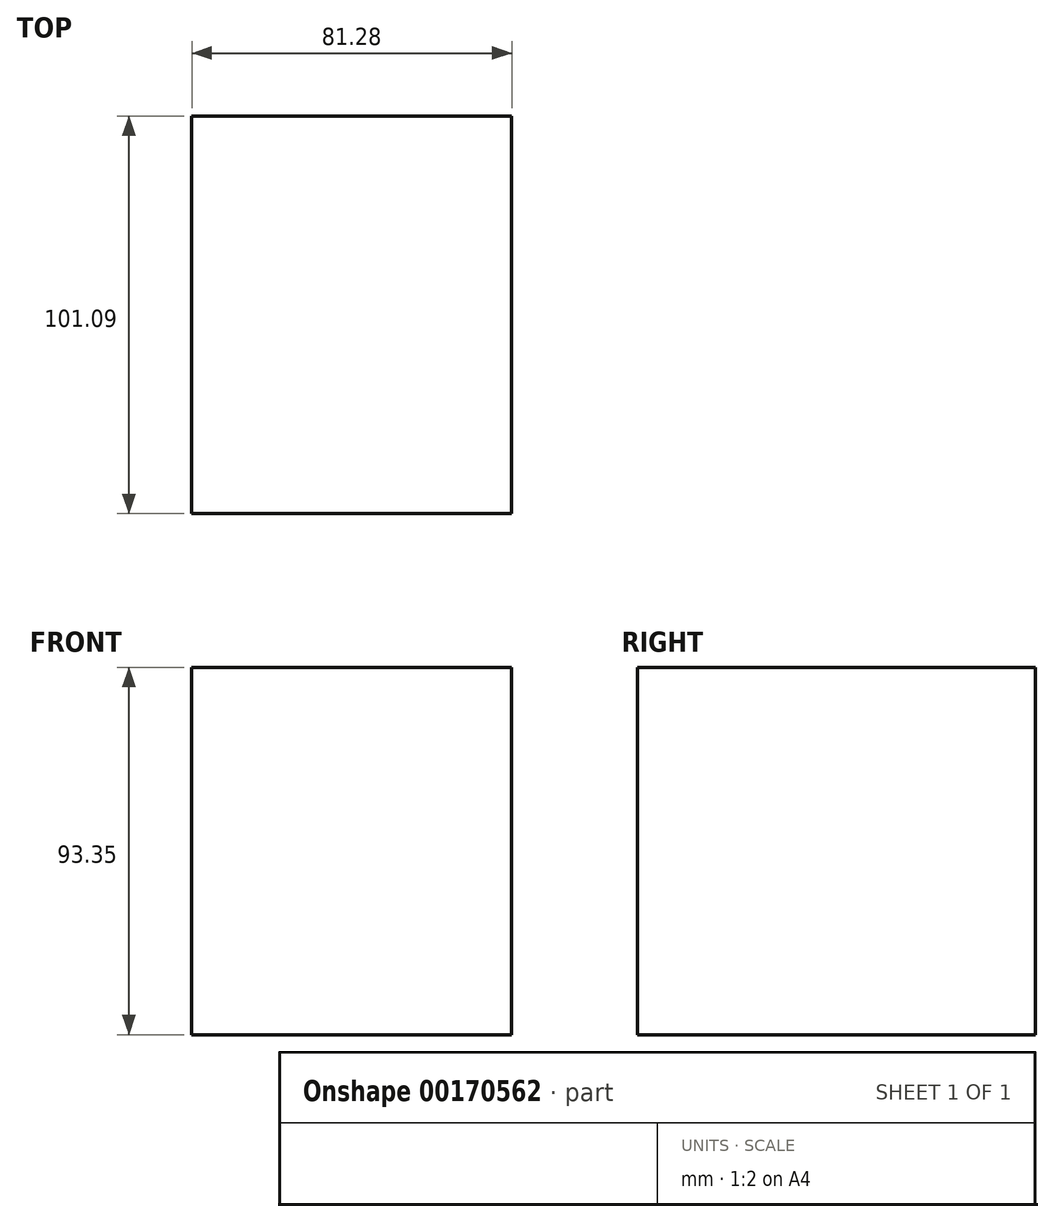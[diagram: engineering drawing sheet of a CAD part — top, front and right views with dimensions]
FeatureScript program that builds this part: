
annotation { "Feature Type Name" : "Feature", "Feature Type Description" : "" }
export const myFeature = defineFeature(function(context is Context, id is Id, definition is map)
    precondition{}
    {
        {
            var Q0;
            Q0=qCreatedBy(makeId("Top.planeOp"),FACE);
            var sketch = newSketch(context, id + "F0", { "sketchPlane" : qUnion([Q0])});
            skLineSegment(sketch, "E0.bottom", {"start": v(-40.24, -33.97) * mm, "end": v(41.04, -33.97) * mm});
            skLineSegment(sketch, "E0.top", {"start": v(-40.24, 67.12) * mm, "end": v(41.04, 67.12) * mm});
            skLineSegment(sketch, "E0.left", {"start": v(-40.24, -33.97) * mm, "end": v(-40.24, 67.12) * mm});
            skLineSegment(sketch, "E0.right", {"start": v(41.04, -33.97) * mm, "end": v(41.04, 67.12) * mm});
            skSolve(sketch);
        }
        {
            var Q0;
            Q0 = qSketchRegion(id + "F0", true);
            extrude(context, id + "F1", {"entities" : qUnion([Q0]), "depth" : 93.35 * mm});
        }
    });
